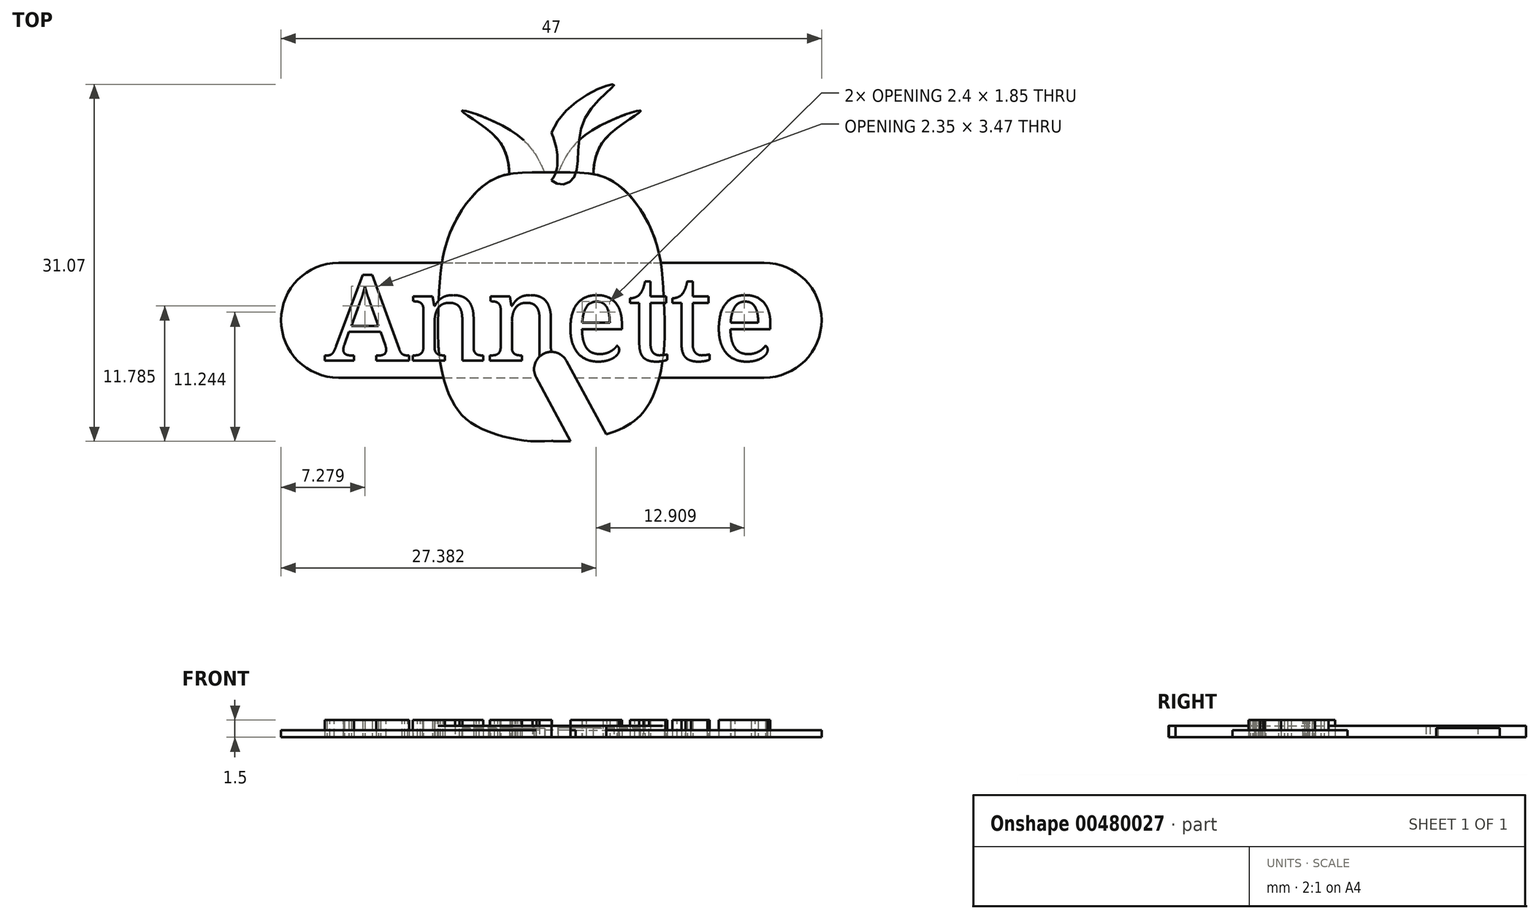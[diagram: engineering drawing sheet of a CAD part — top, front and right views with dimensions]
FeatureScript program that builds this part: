
annotation { "Feature Type Name" : "Feature", "Feature Type Description" : "" }
export const myFeature = defineFeature(function(context is Context, id is Id, definition is map)
    precondition{}
    {
        {
            var Q0;
            Q0=qCreatedBy(makeId("Top.planeOp"),FACE);
            var sketch = newSketch(context, id + "F0", { "sketchPlane" : qUnion([Q0])});
            skText(sketch, "E0", { "text": "Annette", "fontName": "NotoSerif-Regular.ttf"});
            const initialGuessF0  = {"E0": [-0.0197, -0.0075, 1, 0, 0.0075]};
            skSetInitialGuess(sketch, initialGuessF0);
            skSolve(sketch);
        }
        {
            var Q0;
            Q0 = qSketchRegion(id + "F0", true);
            extrude(context, id + "F1", {"entities" : qUnion([Q0]), "depth" : 1.5 * mm, "offsetDistance" : 25 * mm});
        }
        {
            var Q0;
            Q0=qCreatedBy(makeId("Top.planeOp"),FACE);
            var sketch = newSketch(context, id + "F2", { "sketchPlane" : qUnion([Q0])});
            skFitSpline(sketch, "E1", {"points": [v(0, -14.5) * mm, v(-3.65, -14.24) * mm, v(-7.11, -12.83) * mm, v(-8.78, -10.71) * mm, v(-9.74, -7.05) * mm, v(-9.8, -2.69) * mm, v(-9.49, 1.16) * mm, v(-8.52, 4.24) * mm, v(-6.73, 6.94) * mm, v(-4.16, 8.6) * mm, v(0, 8.86) * mm], "startDerivative": vector(-36.01, -3.1) * mm, "endDerivative": vector(39.07, 0.66) * mm});
            skFitSpline(sketch, "E2.MirrorCS", {"points": [v(0, -14.5) * mm, v(3.65, -14.24) * mm, v(7.11, -12.83) * mm, v(8.78, -10.71) * mm, v(9.74, -7.05) * mm, v(9.8, -2.69) * mm, v(9.49, 1.16) * mm, v(8.52, 4.24) * mm, v(6.73, 6.94) * mm, v(4.16, 8.6) * mm, v(0, 8.86) * mm], "startDerivative": vector(36.01, -3.1) * mm, "endDerivative": vector(-39.07, 0.66) * mm});
            skSolve(sketch);
        }
        {
            var Q0;
            Q0=makeQuery(id+"F2.imprint","IMPRINT",FACE,{"disambiguationData":[TD([[makeQuery(id+"F2.imprint","IMPRINT",EDGE,{"derivedFrom":sQuery(id+"F2.wireOp",EDGE,"E1")}),-1.0]])]});
            extrude(context, id + "F3", {"entities" : qUnion([Q0]), "depth" : 1 * mm, "offsetDistance" : 25 * mm});
        }
        {
            var Q0;
            Q0=qCreatedBy(makeId("Top.planeOp"),FACE);
            var sketch = newSketch(context, id + "F4", { "sketchPlane" : qUnion([Q0])});
            skFitSpline(sketch, "E3", {"points": [v(-3.62, 8.13) * mm, v(-4.76, 11.85) * mm, v(-7.76, 14.23) * mm, v(-3.16, 12.26) * mm, v(-0.47, 8.54) * mm], "startDerivative": vector(-0.55, 16.12) * mm, "endDerivative": vector(6.29, -15.12) * mm});
            skLineSegment(sketch, "E4", {"start": v(-3.62, 8.13) * mm, "end": v(-0.47, 8.54) * mm});
            skFitSpline(sketch, "E5.MirrorCS", {"points": [v(3.62, 8.13) * mm, v(4.76, 11.85) * mm, v(7.76, 14.23) * mm, v(3.16, 12.26) * mm, v(0.47, 8.54) * mm], "startDerivative": vector(0.55, 16.12) * mm, "endDerivative": vector(-6.29, -15.12) * mm});
            skLineSegment(sketch, "E6", {"start": v(0.47, 8.54) * mm, "end": v(3.62, 8.13) * mm});
            skSolve(sketch);
        }
        {
            var Q0;
            Q0=makeQuery(id+"F4.imprint","IMPRINT",FACE,{"disambiguationData":[TD([[makeQuery(id+"F4.imprint","IMPRINT",EDGE,{"derivedFrom":sQuery(id+"F4.wireOp",EDGE,"E3")}),-1.0]])]});
            var Q1;
            Q1=makeQuery(id+"F4.imprint","IMPRINT",FACE,{"disambiguationData":[TD([[makeQuery(id+"F4.imprint","IMPRINT",EDGE,{"derivedFrom":sQuery(id+"F4.wireOp",EDGE,"E5.MirrorCS")}),1.0]])]});
            extrude(context, id + "F5", {"entities" : qUnion([Q0, Q1]), "operationType" : NewBodyOperationType.ADD, "depth" : 0.8 * mm, "offsetDistance" : 25 * mm});
        }
        {
            var Q0;
            Q0=qCreatedBy(makeId("Top.planeOp"),FACE);
            var sketch = newSketch(context, id + "F6", { "sketchPlane" : qUnion([Q0])});
            skFitSpline(sketch, "E7", {"points": [v(-1.9, 8.32) * mm, v(-2.9, 13.55) * mm, v(-5.45, 16.5) * mm, v(-0.96, 13.88) * mm, v(0, 8.18) * mm, v(-1.9, 8.32) * mm]});
            skFitSpline(sketch, "E8.MirrorC", {"points": [v(1.9, 8.32) * mm, v(2.9, 13.55) * mm, v(5.45, 16.5) * mm, v(0.96, 13.88) * mm, v(0, 8.18) * mm, v(1.9, 8.32) * mm]});
            skSolve(sketch);
        }
        {
            var Q0;
            {var subQ0=sQuery(id+"F6.wireOp",EDGE,"E8.MirrorC");var subQ1=sQuery(id+"F6.wireOp",EDGE,"E7");var subQ2=makeQuery(id+"F6.imprint","INTERSECT",VERTEX,{"disambiguationData":[OD(0.0)],"derivedFrom":[subQ1,subQ0]});Q0=makeQuery(id+"F6.imprint","IMPRINT",FACE,{"disambiguationData":[TD([[makeQuery(id+"F6.imprint","IMPRINT",EDGE,{"disambiguationData":[TD([[subQ2,-1.0]])],"derivedFrom":subQ1}),-1.0]])]});}
            var Q1;
            {var subQ0=sQuery(id+"F6.wireOp",EDGE,"E8.MirrorC");var subQ1=sQuery(id+"F6.wireOp",EDGE,"E7");var subQ2=makeQuery(id+"F6.imprint","INTERSECT",VERTEX,{"disambiguationData":[OD(0.0)],"derivedFrom":[subQ1,subQ0]});Q1=makeQuery(id+"F6.imprint","IMPRINT",FACE,{"disambiguationData":[TD([[makeQuery(id+"F6.imprint","IMPRINT",EDGE,{"disambiguationData":[TD([[subQ2,1.0]])],"derivedFrom":subQ1}),1.0]])]});}
            extrude(context, id + "F7", {"entities" : qUnion([Q0, Q1]), "depth" : 1 * mm, "offsetDistance" : 25 * mm});
        }
        {
            var Q0;
            Q0=qCreatedBy(makeId("Top.planeOp"),FACE);
            var sketch = newSketch(context, id + "F8", { "sketchPlane" : qUnion([Q0])});
            skLineSegment(sketch, "E9.bottom", {"start": v(-18.5, 1) * mm, "end": v(18.5, 1) * mm});
            skLineSegment(sketch, "E9.top", {"start": v(-18.5, -9) * mm, "end": v(18.5, -9) * mm});
            skArc(sketch, "E10", {"start": v(-18.5, -9) * mm, "mid": v(-23.5, -4) * mm, "end": v(-18.5, 1) * mm});
            skArc(sketch, "E11", {"start": v(18.5, -9) * mm, "mid": v(23.5, -4) * mm, "end": v(18.5, 1) * mm});
            skSolve(sketch);
        }
        {
            var Q0;
            Q0=makeQuery(id+"F8.imprint","IMPRINT",FACE,{"disambiguationData":[TD([[makeQuery(id+"F8.imprint","IMPRINT",EDGE,{"derivedFrom":sQuery(id+"F8.wireOp",EDGE,"E9.bottom")}),-1.0]])]});
            extrude(context, id + "F9", {"entities" : qUnion([Q0]), "depth" : 0.6 * mm, "offsetDistance" : 25 * mm});
        }
        {
            var Q0;
            Q0=qCreatedBy(makeId("Top.planeOp"),FACE);
            var sketch = newSketch(context, id + "F10", { "sketchPlane" : qUnion([Q0])});
            skLineSegment(sketch, "E12", {"start": v(3.92, -18.7) * mm, "end": v(-1.32, -8.97) * mm});
            skLineSegment(sketch, "E13", {"start": v(-1.32, -8.97) * mm, "end": v(1.32, -7.55) * mm, "construction": true});
            skLineSegment(sketch, "E14", {"start": v(1.32, -7.55) * mm, "end": v(6.54, -17.23) * mm});
            skLineSegment(sketch, "E15", {"start": v(6.54, -17.23) * mm, "end": v(3.92, -18.7) * mm});
            skArc(sketch, "E16", {"start": v(-1.32, -8.97) * mm, "mid": v(-0.71, -6.94) * mm, "end": v(1.32, -7.55) * mm});
            skSolve(sketch);
        }
        {
            var Q0;
            Q0=makeQuery(id+"F10.imprint","IMPRINT",FACE,{"disambiguationData":[TD([[makeQuery(id+"F10.imprint","IMPRINT",EDGE,{"derivedFrom":sQuery(id+"F10.wireOp",EDGE,"E12")}),-1.0]])]});
            extrude(context, id + "F11", {"entities" : qUnion([Q0]), "operationType" : NewBodyOperationType.REMOVE, "depth" : 25 * mm, "offsetDistance" : 25 * mm});
        }
    });
